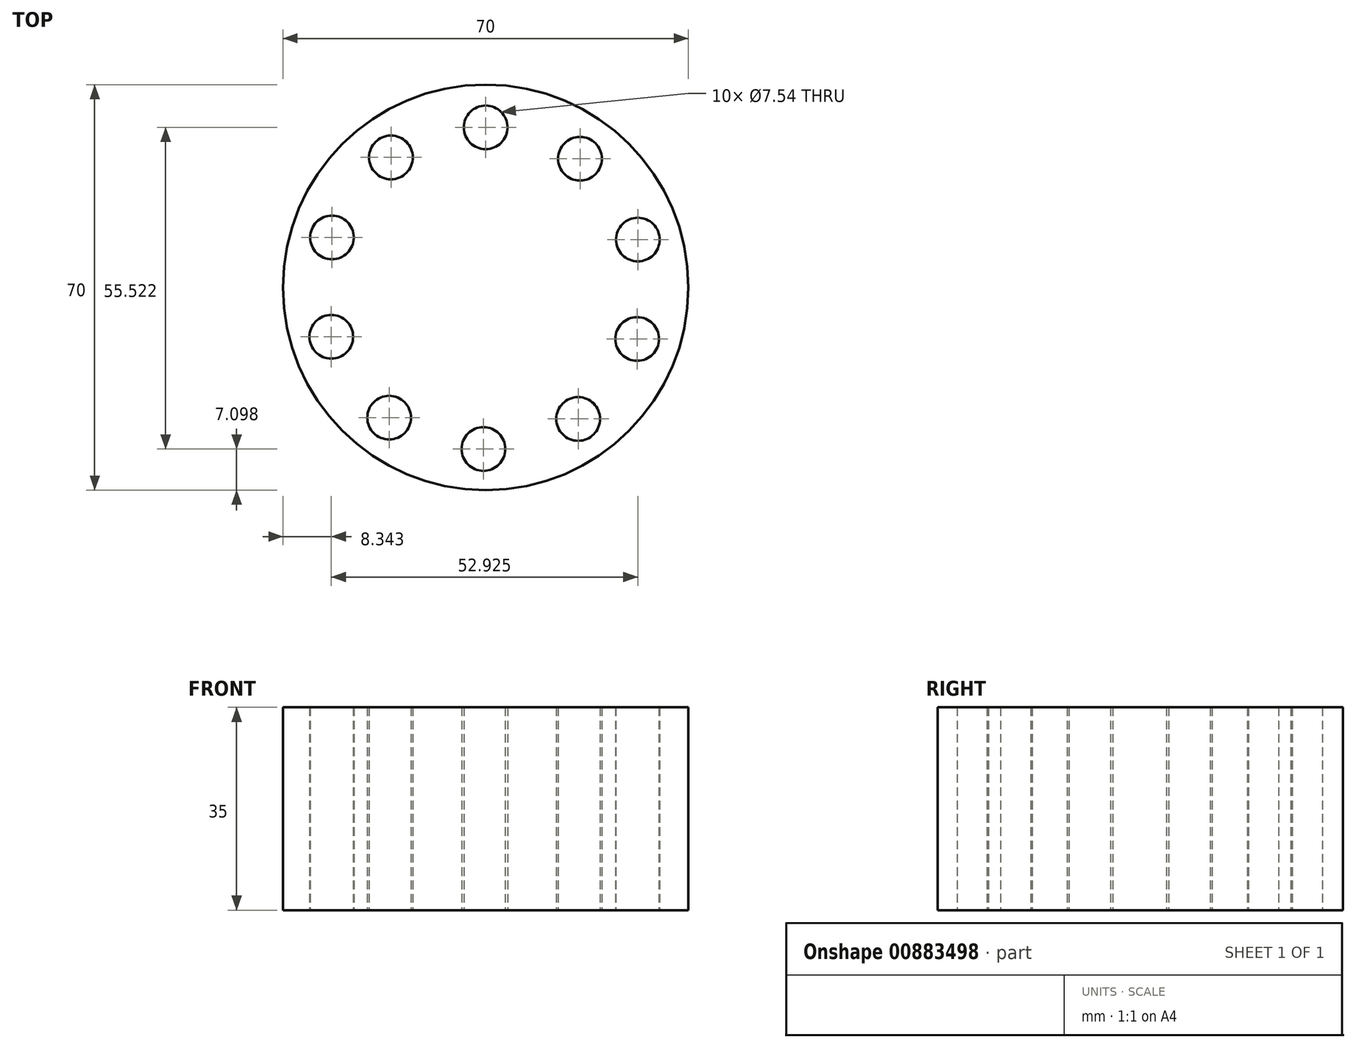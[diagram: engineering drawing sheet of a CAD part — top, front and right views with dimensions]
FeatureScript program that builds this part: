
annotation { "Feature Type Name" : "Feature", "Feature Type Description" : "" }
export const myFeature = defineFeature(function(context is Context, id is Id, definition is map)
    precondition{}
    {
        {
            var Q0;
            Q0=qCreatedBy(makeId("Top.planeOp"),FACE);
            var sketch = newSketch(context, id + "F0", { "sketchPlane" : qUnion([Q0])});
            skCircle(sketch, "E0", {"center": v(0, 0) * mm, "radius": 35 * mm});
            skCircle(sketch, "E1", {"center": v(0, 27.62) * mm, "radius": 3.77 * mm});
            skCircle(sketch, "E2.1.0", {"center": v(-16.35, 22.43) * mm, "radius": 3.77 * mm});
            skCircle(sketch, "E2.2.0", {"center": v(-26.54, 8.62) * mm, "radius": 3.77 * mm});
            skCircle(sketch, "E2.3.0", {"center": v(-26.66, -8.53) * mm, "radius": 3.77 * mm});
            skCircle(sketch, "E2.4.0", {"center": v(-16.67, -22.49) * mm, "radius": 3.77 * mm});
            skCircle(sketch, "E2.5.0", {"center": v(-0.39, -27.9) * mm, "radius": 3.77 * mm});
            skCircle(sketch, "E2.6.0", {"center": v(15.96, -22.72) * mm, "radius": 3.77 * mm});
            skCircle(sketch, "E2.7.0", {"center": v(26.15, -8.9) * mm, "radius": 3.77 * mm});
            skCircle(sketch, "E2.8.0", {"center": v(26.27, 8.25) * mm, "radius": 3.77 * mm});
            skCircle(sketch, "E2.9.0", {"center": v(16.28, 22.2) * mm, "radius": 3.77 * mm});
            skPoint(sketch, "E2.center", {"position": v(-0.2, -0.14) * mm});
            skSolve(sketch);
        }
        {
            var Q0;
            Q0 = qSketchRegion(id + "F0", true);
            extrude(context, id + "F1", {"entities" : qUnion([Q0]), "depth" : 35 * mm, "offsetDistance" : 25 * mm});
        }
        {
            var Q0;
            Q0 = qSketchRegion(id + "F0", true);
            extrude(context, id + "F2", {"entities" : qUnion([Q0]), "operationType" : NewBodyOperationType.ADD, "depth" : 25 * mm, "offsetDistance" : 25 * mm});
        }
    });
